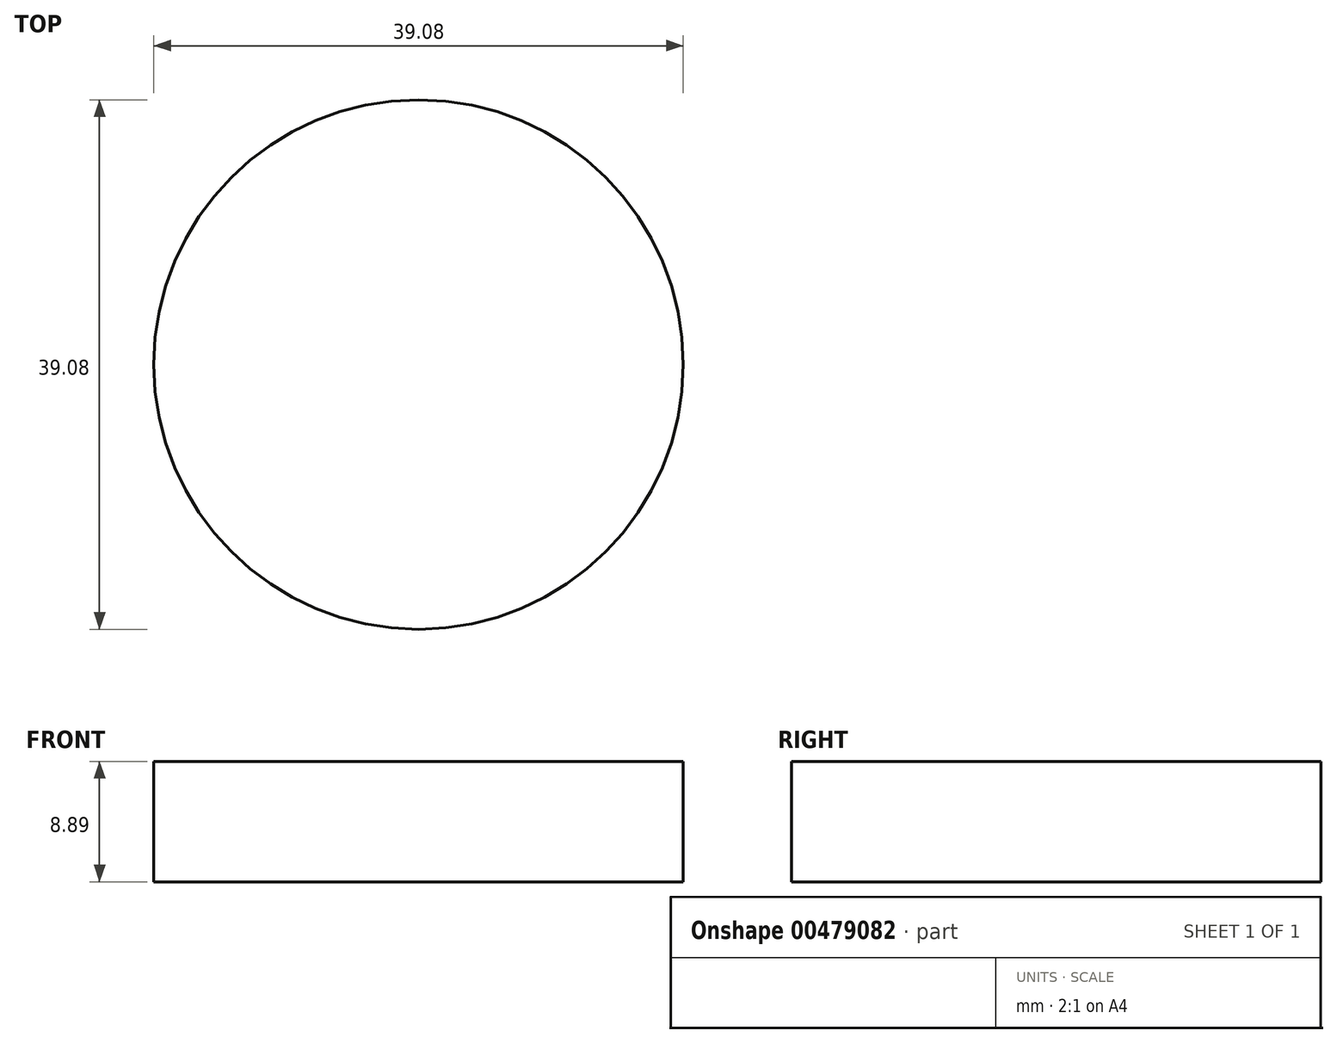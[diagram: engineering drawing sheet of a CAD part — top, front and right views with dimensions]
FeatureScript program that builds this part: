
annotation { "Feature Type Name" : "Feature", "Feature Type Description" : "" }
export const myFeature = defineFeature(function(context is Context, id is Id, definition is map)
    precondition{}
    {
        {
            var Q0;
            Q0=qCreatedBy(makeId("Top.planeOp"),FACE);
            var sketch = newSketch(context, id + "F0", { "sketchPlane" : qUnion([Q0])});
            skCircle(sketch, "E0", {"center": v(0, 0) * mm, "radius": 19.54 * mm});
            skSolve(sketch);
        }
        {
            var Q0;
            Q0 = qSketchRegion(id + "F0", true);
            extrude(context, id + "F1", {"entities" : qUnion([Q0]), "depth" : 8.9 * mm});
        }
    });
